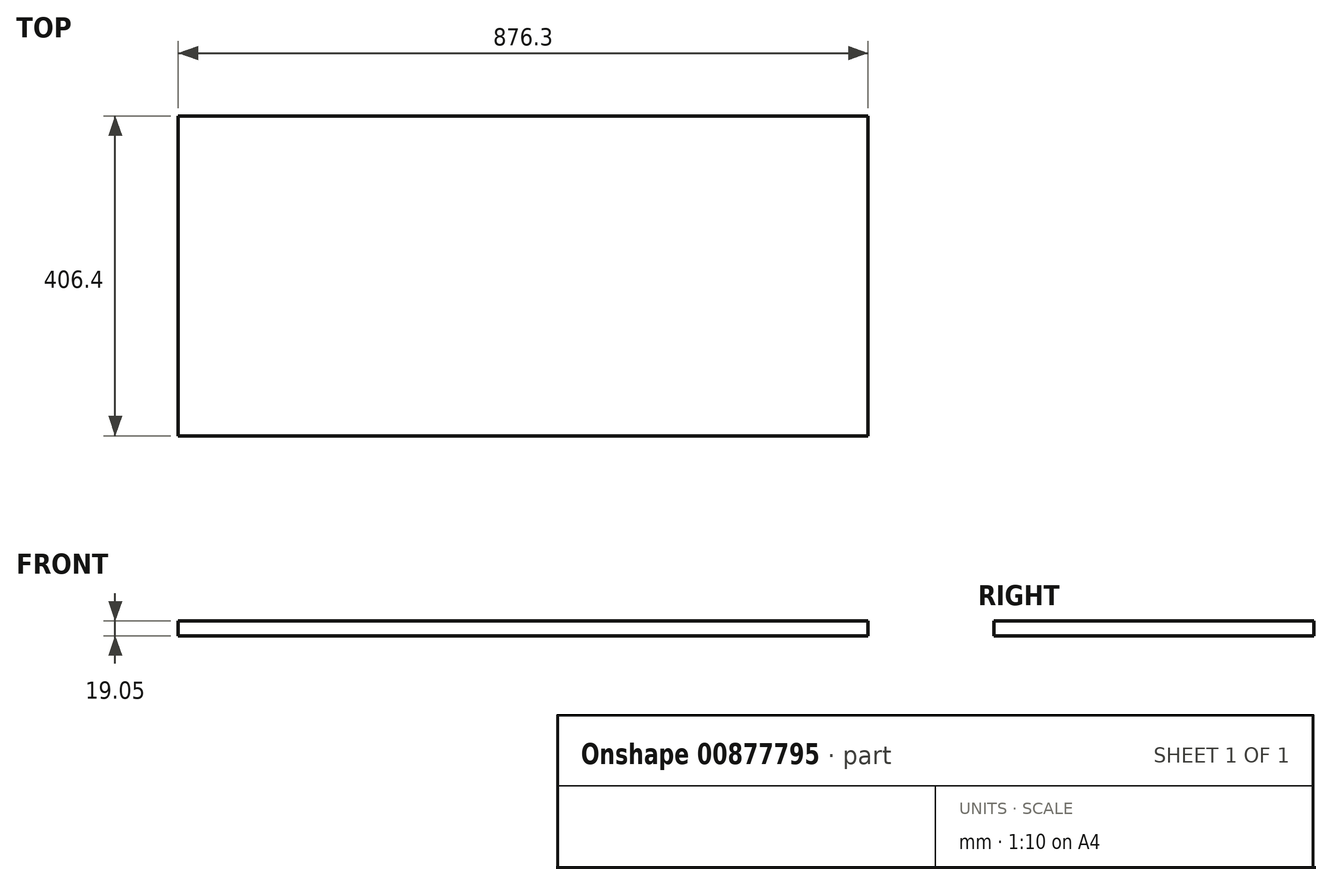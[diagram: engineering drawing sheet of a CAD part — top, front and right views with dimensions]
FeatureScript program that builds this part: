
annotation { "Feature Type Name" : "Feature", "Feature Type Description" : "" }
export const myFeature = defineFeature(function(context is Context, id is Id, definition is map)
    precondition{}
    {
        {
            var Q0;
            Q0=qCreatedBy(makeId("Top.planeOp"),FACE);
            var sketch = newSketch(context, id + "F0", { "sketchPlane" : qUnion([Q0])});
            skLineSegment(sketch, "E0.bottom", {"start": v(-439.64, 36.38) * mm, "end": v(436.66, 36.38) * mm});
            skLineSegment(sketch, "E0.top", {"start": v(-439.64, -370.02) * mm, "end": v(436.66, -370.02) * mm});
            skLineSegment(sketch, "E0.left", {"start": v(-439.64, 36.38) * mm, "end": v(-439.64, -370.02) * mm});
            skLineSegment(sketch, "E0.right", {"start": v(436.66, 36.38) * mm, "end": v(436.66, -370.02) * mm});
            skSolve(sketch);
        }
        {
            var Q0;
            Q0=makeQuery(id+"F0.imprint","IMPRINT",FACE,{"disambiguationData":[TD([[makeQuery(id+"F0.imprint","IMPRINT",EDGE,{"derivedFrom":sQuery(id+"F0.wireOp",EDGE,"E0.bottom")}),-1.0]])]});
            extrude(context, id + "F1", {"entities" : qUnion([Q0]), "depth" : 19.05 * mm, "offsetDistance" : 25.4 * mm});
        }
    });
